# Revit family: Door-Hdwr_Entry-Decor
name_source: partatom
category: Doors
units: mm (PartAtom-declared; Revit-internal decimal feet)

## family parameters
Classification Number = 23.30.40.11.31
Cut with Voids When Loaded = No
Host = Face
Room Calculation Point = No
Shared = Yes

## types (1)
- Door-Hdwr_Entry-Decor
    ANSI Conformance = A156.2
    Assembly Code = C1020410
    Construction Details = http://www.arcat.com
    Deadbolt Strike Type = Recessed Cup Security Strike
    Deadbolt Throw = 0' - 1"
    Default Elevation = 4' - 0"
    Description = Entry Door Hardware - Decorative
    Door Hardware UL Listed = Yes
    Door Slab Thickness = 0' - 1 7/8"
    Expected Lifespan (Years) = 0
    Function = Interior
    Height = 0' - 1 7/16"
    Keynote = 08710
    Latch Strike Type = Curved Lip
    Lock Cylinder Finish = ARCAT - Metal - Brass, Polished
    Lock Cylinder Pin Count = 6
    Lock Cylinder Type = Keyed Exterior - Thumbturn Interior
    Maintenance Schedule (Months) = 0
    Manufacturer = Generic
    Manufacturer Fax = (203) 929-2444
    Manufacturer Website = http://www.arcat.com
    Model = Generic
    Operation = Manual Locking
    Product Data = http://www.arcat.com
    Product Properties = http://www.arcat.com
    Specification = http://www.arcat.com
    Warranty Duration (Years) = 0
    boltloc = 0' - 0 23/32"
    ltchloc = 0' - 0 7/16"

## geometry (parser evidence)
native form markers: Sweep x3
no freeform markers — native parametric forms only
